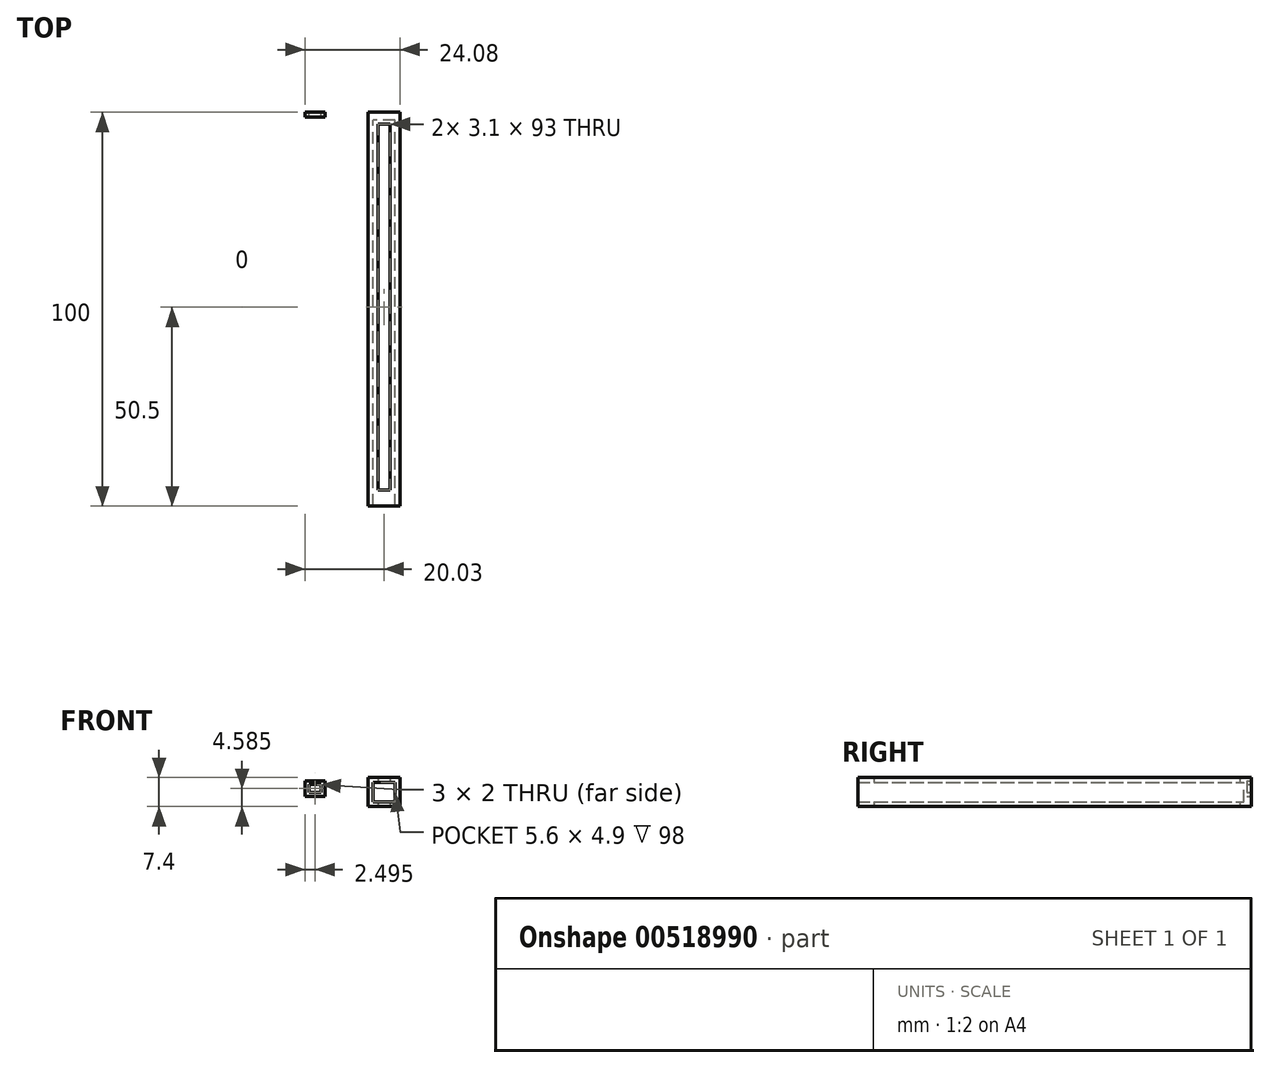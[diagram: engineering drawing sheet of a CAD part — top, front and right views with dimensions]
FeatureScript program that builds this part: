
annotation { "Feature Type Name" : "Feature", "Feature Type Description" : "" }
export const myFeature = defineFeature(function(context is Context, id is Id, definition is map)
    precondition{}
    {
        {
            var Q0;
            Q0=qCreatedBy(makeId("Front.planeOp"),FACE);
            var sketch = newSketch(context, id + "F0", { "sketchPlane" : qUnion([Q0])});
            skLineSegment(sketch, "E0.bottom", {"start": v(1.25, 6.15) * mm, "end": v(6.85, 6.15) * mm});
            skLineSegment(sketch, "E0.top", {"start": v(1.25, 1.25) * mm, "end": v(6.85, 1.25) * mm});
            skLineSegment(sketch, "E0.left", {"start": v(1.25, 6.15) * mm, "end": v(1.25, 1.25) * mm});
            skLineSegment(sketch, "E0.right", {"start": v(6.85, 6.15) * mm, "end": v(6.85, 1.25) * mm});
            skLineSegment(sketch, "E1.bottom", {"start": v(0, 7.4) * mm, "end": v(8.1, 7.4) * mm});
            skLineSegment(sketch, "E1.top", {"start": v(0, 0) * mm, "end": v(8.1, 0) * mm});
            skLineSegment(sketch, "E1.left", {"start": v(0, 7.4) * mm, "end": v(0, 0) * mm});
            skLineSegment(sketch, "E1.right", {"start": v(8.1, 7.4) * mm, "end": v(8.1, 0) * mm});
            skLineSegment(sketch, "E2", {"start": v(8.1, 1.77) * mm, "end": v(6.85, 1.77) * mm, "construction": true});
            skLineSegment(sketch, "E3", {"start": v(1.25, 1.77) * mm, "end": v(0, 1.77) * mm, "construction": true});
            skLineSegment(sketch, "E4", {"start": v(0.55, 6.15) * mm, "end": v(0.55, 7.4) * mm, "construction": true});
            skLineSegment(sketch, "E5", {"start": v(0.74, 1.25) * mm, "end": v(0.74, 0) * mm, "construction": true});
            skPoint(sketch, "E5.endSnap0", {"position": v(4.05, 0) * mm});
            skSolve(sketch);
        }
        {
            var Q0;
            Q0=makeQuery(id+"F0.imprint","IMPRINT",FACE,{"disambiguationData":[TD([[makeQuery(id+"F0.imprint","IMPRINT",EDGE,{"derivedFrom":sQuery(id+"F0.wireOp",EDGE,"E0.bottom")}),1.0]])]});
            var Q1;
            Q1=makeQuery(id+"F0.imprint","IMPRINT",FACE,{"disambiguationData":[TD([[makeQuery(id+"F0.imprint","IMPRINT",EDGE,{"derivedFrom":sQuery(id+"F0.wireOp",EDGE,"E0.bottom")}),-1.0]])]});
            extrude(context, id + "F1", {"entities" : qUnion([Q0, Q1]), "depth" : 2 * mm, "offsetDistance" : 25 * mm});
        }
        {
            var Q0;
            Q0 = qSketchRegion(id + "F0", true);
            extrude(context, id + "F2", {"entities" : qUnion([Q0]), "operationType" : NewBodyOperationType.ADD, "depth" : 100 * mm, "offsetDistance" : 25 * mm});
        }
        {
            var Q0;
            {var subQ0=sQuery(id+"F0.wireOp",EDGE,"E1.top");Q0=makeQuery(id+"F2.boolean.opBoolean","MERGE",FACE,{"derivedFrom":[makeQuery(id+"F1.opExtrude","SWEPT_FACE",FACE,{"disambiguationData":[OSD([subQ0])]}),makeQuery(id+"F2.opExtrude","SWEPT_FACE",FACE,{"disambiguationData":[OSD([subQ0])]})]});}
            var sketch = newSketch(context, id + "F3", { "sketchPlane" : qUnion([Q0])});
            skLineSegment(sketch, "E6.bottom", {"start": v(2.5, 3) * mm, "end": v(5.6, 3) * mm});
            skLineSegment(sketch, "E6.top", {"start": v(2.5, 96) * mm, "end": v(5.6, 96) * mm});
            skLineSegment(sketch, "E6.left", {"start": v(2.5, 3) * mm, "end": v(2.5, 96) * mm});
            skLineSegment(sketch, "E6.right", {"start": v(5.6, 3) * mm, "end": v(5.6, 96) * mm});
            skSolve(sketch);
        }
        {
            var Q0;
            Q0=makeQuery(id+"F3.imprint","IMPRINT",FACE,{"disambiguationData":[TD([[makeQuery(id+"F3.imprint","IMPRINT",EDGE,{"derivedFrom":sQuery(id+"F3.wireOp",EDGE,"E6.bottom")}),1.0]])]});
            extrude(context, id + "F4", {"entities" : qUnion([Q0]), "operationType" : NewBodyOperationType.REMOVE, "oppositeDirection" : true, "depth" : 25 * mm, "offsetDistance" : 25 * mm});
        }
        {
            var Q0;
            {var subQ0=sQuery(id+"F0.wireOp",EDGE,"E1.left");Q0=makeQuery(id+"F2.boolean.opBoolean","MERGE",FACE,{"derivedFrom":[makeQuery(id+"F1.opExtrude","SWEPT_FACE",FACE,{"disambiguationData":[OSD([subQ0])]}),makeQuery(id+"F2.opExtrude","SWEPT_FACE",FACE,{"disambiguationData":[OSD([subQ0])]})]});}
            var sketch = newSketch(context, id + "F5", { "sketchPlane" : qUnion([Q0])});
            skLineSegment(sketch, "E7.bottom", {"start": v(52.8, 5.4) * mm, "end": v(3, 5.4) * mm});
            skLineSegment(sketch, "E7.top", {"start": v(52.8, 2) * mm, "end": v(3, 2) * mm});
            skLineSegment(sketch, "E7.left", {"start": v(52.8, 5.4) * mm, "end": v(52.8, 2) * mm});
            skLineSegment(sketch, "E7.right", {"start": v(3, 5.4) * mm, "end": v(3, 2) * mm});
            skSolve(sketch);
        }
        {
            var Q0;
            Q0=qCreatedBy(makeId("Front.planeOp"),FACE);
            var sketch = newSketch(context, id + "F6", { "sketchPlane" : qUnion([Q0])});
            skLineSegment(sketch, "E8.bottom", {"start": v(-15.98, 6.58) * mm, "end": v(-10.98, 6.58) * mm});
            skLineSegment(sketch, "E8.top", {"start": v(-15.98, 2.58) * mm, "end": v(-10.98, 2.58) * mm});
            skLineSegment(sketch, "E8.left", {"start": v(-15.98, 6.58) * mm, "end": v(-15.98, 2.58) * mm});
            skLineSegment(sketch, "E8.right", {"start": v(-10.98, 6.58) * mm, "end": v(-10.98, 2.58) * mm});
            skLineSegment(sketch, "E9.bottom", {"start": v(-14.98, 5.58) * mm, "end": v(-11.98, 5.58) * mm});
            skLineSegment(sketch, "E9.top", {"start": v(-14.98, 3.58) * mm, "end": v(-11.98, 3.58) * mm});
            skLineSegment(sketch, "E9.left", {"start": v(-14.98, 5.58) * mm, "end": v(-14.98, 3.58) * mm});
            skLineSegment(sketch, "E9.right", {"start": v(-11.98, 5.58) * mm, "end": v(-11.98, 3.58) * mm});
            skSolve(sketch);
        }
        {
            var Q0;
            Q0=makeQuery(id+"F6.imprint","IMPRINT",FACE,{"disambiguationData":[TD([[makeQuery(id+"F6.imprint","IMPRINT",EDGE,{"derivedFrom":sQuery(id+"F6.wireOp",EDGE,"E8.bottom")}),-1.0]])]});
            extrude(context, id + "F7", {"entities" : qUnion([Q0]), "depth" : 1.25 * mm, "offsetDistance" : 25 * mm});
        }
    });
